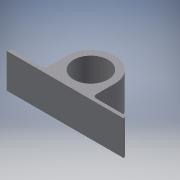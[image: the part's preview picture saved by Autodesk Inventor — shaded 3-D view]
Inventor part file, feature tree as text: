
AUTODESK INVENTOR PART (.ipt)
format: ipt  version: 2017 (Build 210142000, 142)  size: 120,320 bytes
history: native  units: mm
features: other x3, extrude x1, sketch x1, reference x1
ambient origin geometry x8: Origin, YZ Plane, XZ Plane, XY Plane, X Axis, Y Axis, Z Axis, Center Point
bodies: Solid1 (feature_tree)
feature tree (6):
  extrude  "Extrusion1"  Depth=2.0mm
  sketch  "Sketch1"  dims[d0=20.0mm d1=2.0mm d2=4.0mm d3=20.0mm d4=20.0mm d5=15.0mm d6=150.0mm d7=2.0mm d8=20.0mm d9=0.0mm]
  reference  "Reference1"
  parser-record x1  (decoder bookkeeping rows leaked as tree rows — omitted from the tree; the rows remain in map.json)
  other  "VolledigGeassembleerdv001.iam"
  other  "Frame:1"
note: 1 file-system path scrubbed to <path> (originals preserved in map.json)
